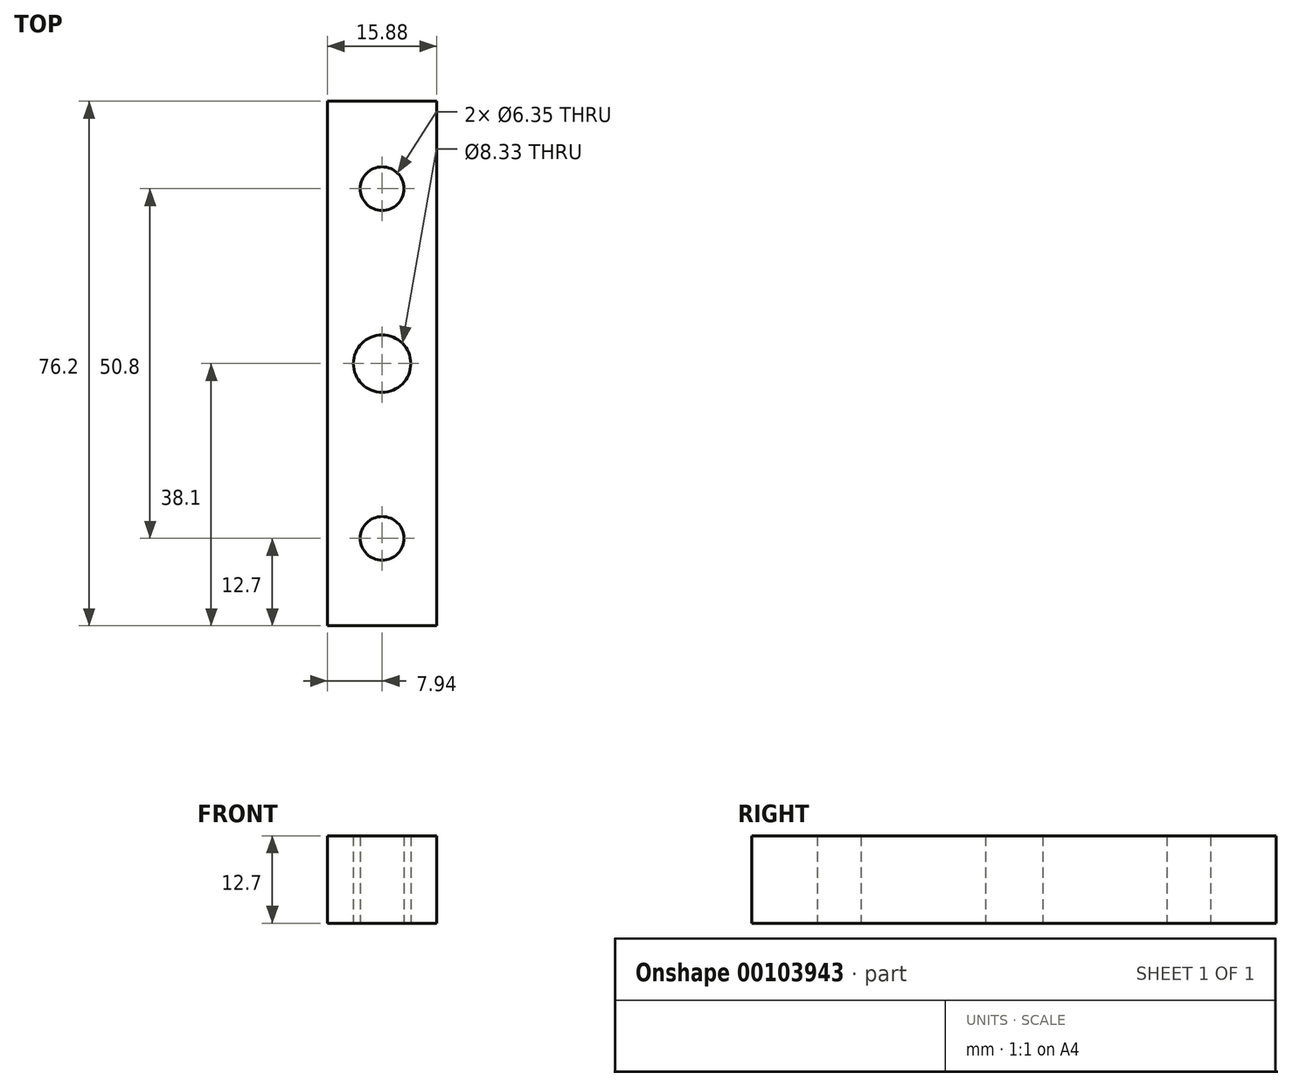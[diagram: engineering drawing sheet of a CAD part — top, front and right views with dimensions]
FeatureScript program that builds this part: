
annotation { "Feature Type Name" : "Feature", "Feature Type Description" : "" }
export const myFeature = defineFeature(function(context is Context, id is Id, definition is map)
    precondition{}
    {
        {
            var Q0;
            Q0=qCreatedBy(makeId("Top.planeOp"),FACE);
            var sketch = newSketch(context, id + "F0", { "sketchPlane" : qUnion([Q0])});
            skLineSegment(sketch, "E0.bottom", {"start": v(-7.94, 38.1) * mm, "end": v(7.94, 38.1) * mm});
            skLineSegment(sketch, "E0.top", {"start": v(-7.94, -38.1) * mm, "end": v(7.94, -38.1) * mm});
            skLineSegment(sketch, "E0.left", {"start": v(-7.94, 38.1) * mm, "end": v(-7.94, -38.1) * mm});
            skLineSegment(sketch, "E0.right", {"start": v(7.94, 38.1) * mm, "end": v(7.94, -38.1) * mm});
            skCircle(sketch, "E1", {"center": v(0, 25.4) * mm, "radius": 3.18 * mm});
            skLineSegment(sketch, "E2", {"start": v(-7.94, 0) * mm, "end": v(7.94, 0) * mm, "construction": true});
            skCircle(sketch, "E3.MirrorC", {"center": v(0, -25.4) * mm, "radius": 3.18 * mm});
            skCircle(sketch, "E4", {"center": v(0, 0) * mm, "radius": 4.17 * mm});
            skSolve(sketch);
        }
        {
            var Q0;
            Q0=qSketchRegion(id+"F0",true);
            extrude(context, id + "F1", {"entities" : qUnion([Q0]), "depth" : 12.7 * mm});
        }
    });
